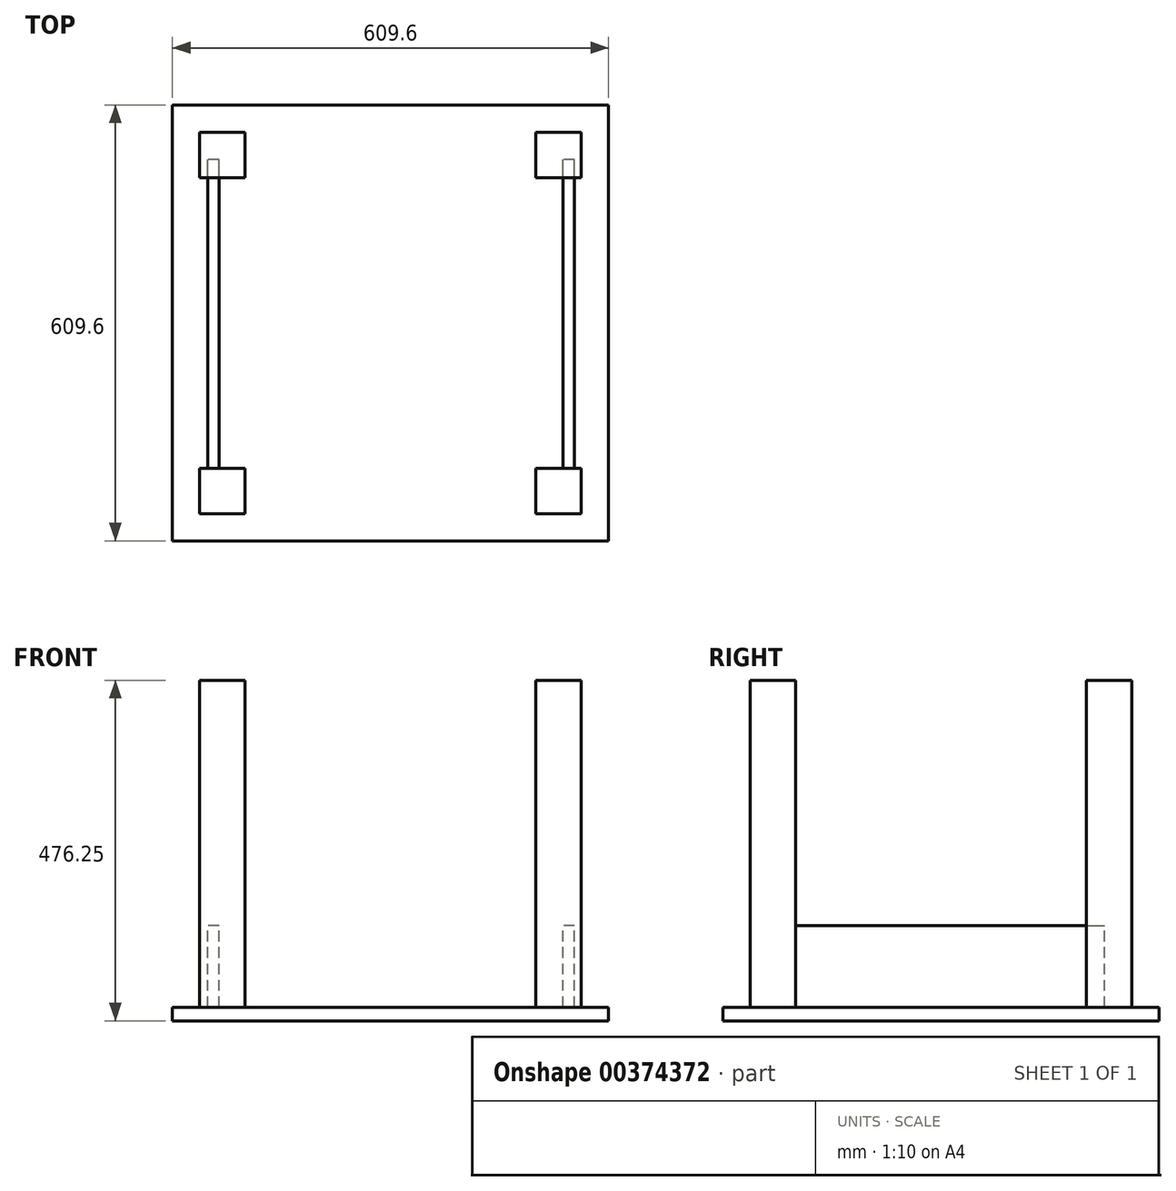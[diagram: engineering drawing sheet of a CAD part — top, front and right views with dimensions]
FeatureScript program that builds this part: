
annotation { "Feature Type Name" : "Feature", "Feature Type Description" : "" }
export const myFeature = defineFeature(function(context is Context, id is Id, definition is map)
    precondition{}
    {
        {
            var Q0;
            Q0=qCreatedBy(makeId("Front.planeOp"),FACE);
            var sketch = newSketch(context, id + "F0", { "sketchPlane" : qUnion([Q0])});
            skLineSegment(sketch, "E0.bottom", {"start": v(-303.33, -19.05) * mm, "end": v(306.27, -19.05) * mm});
            skLineSegment(sketch, "E0.top", {"start": v(-303.33, 0) * mm, "end": v(306.27, 0) * mm});
            skLineSegment(sketch, "E0.left", {"start": v(-303.33, -19.05) * mm, "end": v(-303.33, 0) * mm});
            skLineSegment(sketch, "E0.right", {"start": v(306.27, -19.05) * mm, "end": v(306.27, 0) * mm});
            skLineSegment(sketch, "E1.bottom", {"start": v(306.27, 0) * mm, "end": v(306.27, 0) * mm});
            skLineSegment(sketch, "E1.top", {"start": v(306.27, -19.05) * mm, "end": v(306.27, -19.05) * mm});
            skLineSegment(sketch, "E1.left", {"start": v(306.27, 0) * mm, "end": v(306.27, -19.05) * mm});
            skLineSegment(sketch, "E1.right", {"start": v(306.27, 0) * mm, "end": v(306.27, -19.05) * mm});
            skSolve(sketch);
        }
        {
            var Q0;
            Q0=makeQuery(id+"F0.imprint","IMPRINT",FACE,{"disambiguationData":[TD([[makeQuery(id+"F0.imprint","IMPRINT",EDGE,{"derivedFrom":sQuery(id+"F0.wireOp",EDGE,"E0.bottom")}),1.0]])]});
            extrude(context, id + "F1", {"entities" : qUnion([Q0]), "depth" : 609.6 * mm});
        }
        {
            var Q0;
            Q0=makeQuery(id+"F1.opExtrude","SWEPT_FACE",FACE,{"disambiguationData":[OSD([sQuery(id+"F0.wireOp",EDGE,"E0.top")])]});
            var sketch = newSketch(context, id + "F2", { "sketchPlane" : qUnion([Q0])});
            skLineSegment(sketch, "E2.bottom", {"start": v(-265.23, -571.5) * mm, "end": v(-201.73, -571.5) * mm});
            skLineSegment(sketch, "E2.top", {"start": v(-265.23, -508) * mm, "end": v(-201.73, -508) * mm});
            skLineSegment(sketch, "E2.left", {"start": v(-265.23, -571.5) * mm, "end": v(-265.23, -508) * mm});
            skLineSegment(sketch, "E2.right", {"start": v(-201.73, -571.5) * mm, "end": v(-201.73, -508) * mm});
            skLineSegment(sketch, "E3.bottom", {"start": v(-265.23, -38.1) * mm, "end": v(-201.73, -38.1) * mm});
            skLineSegment(sketch, "E3.top", {"start": v(-265.23, -101.6) * mm, "end": v(-201.73, -101.6) * mm});
            skLineSegment(sketch, "E3.left", {"start": v(-265.23, -38.1) * mm, "end": v(-265.23, -101.6) * mm});
            skLineSegment(sketch, "E3.right", {"start": v(-201.73, -38.1) * mm, "end": v(-201.73, -101.6) * mm});
            skLineSegment(sketch, "E4.bottom", {"start": v(268.17, -38.1) * mm, "end": v(204.67, -38.1) * mm});
            skLineSegment(sketch, "E4.top", {"start": v(268.17, -101.6) * mm, "end": v(204.67, -101.6) * mm});
            skLineSegment(sketch, "E4.left", {"start": v(268.17, -38.1) * mm, "end": v(268.17, -101.6) * mm});
            skLineSegment(sketch, "E4.right", {"start": v(204.67, -38.1) * mm, "end": v(204.67, -101.6) * mm});
            skLineSegment(sketch, "E5.bottom", {"start": v(268.17, -571.5) * mm, "end": v(204.67, -571.5) * mm});
            skLineSegment(sketch, "E5.top", {"start": v(268.17, -508) * mm, "end": v(204.67, -508) * mm});
            skLineSegment(sketch, "E5.left", {"start": v(268.17, -571.5) * mm, "end": v(268.17, -508) * mm});
            skLineSegment(sketch, "E5.right", {"start": v(204.67, -571.5) * mm, "end": v(204.67, -508) * mm});
            skSolve(sketch);
        }
        {
            var Q0;
            Q0=makeQuery(id+"F2.imprint","IMPRINT",FACE,{"disambiguationData":[TD([[makeQuery(id+"F2.imprint","IMPRINT",EDGE,{"derivedFrom":sQuery(id+"F2.wireOp",EDGE,"E2.bottom")}),1.0]])]});
            var Q1;
            Q1=makeQuery(id+"F2.imprint","IMPRINT",FACE,{"disambiguationData":[TD([[makeQuery(id+"F2.imprint","IMPRINT",EDGE,{"derivedFrom":sQuery(id+"F2.wireOp",EDGE,"E3.bottom")}),-1.0]])]});
            var Q2;
            Q2=makeQuery(id+"F2.imprint","IMPRINT",FACE,{"disambiguationData":[TD([[makeQuery(id+"F2.imprint","IMPRINT",EDGE,{"derivedFrom":sQuery(id+"F2.wireOp",EDGE,"E4.bottom")}),1.0]])]});
            var Q3;
            Q3=makeQuery(id+"F2.imprint","IMPRINT",FACE,{"disambiguationData":[TD([[makeQuery(id+"F2.imprint","IMPRINT",EDGE,{"derivedFrom":sQuery(id+"F2.wireOp",EDGE,"E5.bottom")}),-1.0]])]});
            extrude(context, id + "F3", {"entities" : qUnion([Q0, Q1, Q2, Q3]), "depth" : 457.2 * mm});
        }
        {
            var Q0;
            Q0=makeQuery(id+"F3.opExtrude","SWEPT_FACE",FACE,{"disambiguationData":[OSD([sQuery(id+"F2.wireOp",EDGE,"E4.top")])]});
            var sketch = newSketch(context, id + "F4", { "sketchPlane" : qUnion([Q0])});
            skLineSegment(sketch, "E6.bottom", {"start": v(258.64, 0) * mm, "end": v(242.77, 0) * mm});
            skLineSegment(sketch, "E6.top", {"start": v(258.64, 114.3) * mm, "end": v(242.77, 114.3) * mm});
            skLineSegment(sketch, "E6.left", {"start": v(258.64, 0) * mm, "end": v(258.64, 114.3) * mm});
            skLineSegment(sketch, "E6.right", {"start": v(242.77, 0) * mm, "end": v(242.77, 114.3) * mm});
            skSolve(sketch);
        }
        {
            var Q0;
            Q0=makeQuery(id+"F4.imprint","IMPRINT",FACE,{"disambiguationData":[TD([[makeQuery(id+"F4.imprint","IMPRINT",EDGE,{"derivedFrom":sQuery(id+"F4.wireOp",EDGE,"E6.bottom")}),-1.0]])]});
            extrude(context, id + "F5", {"entities" : qUnion([Q0]), "endBound" : BoundingType.UP_TO_NEXT, "depth" : 326.18 * mm, "hasSecondDirection" : true, "secondDirectionOppositeDirection" : true, "secondDirectionDepth" : 25.4 * mm});
        }
        {
            var Q0;
            Q0=makeQuery(id+"F5.opExtrude","SWEPT_BODY",BODY,{"disambiguationData":[OSD([sQuery(id+"F4.wireOp",EDGE,"E6.bottom"),sQuery(id+"F4.wireOp",EDGE,"E6.top"),sQuery(id+"F4.wireOp",EDGE,"E6.left"),sQuery(id+"F4.wireOp",EDGE,"E6.right")])]});
            transform(context, id + "F6", {"entities" : qUnion([Q0]), "transformType" : TransformType.TRANSLATION_3D, "dx" : -496.92 * mm, "dy" : 0 * mm, "dz" : 0 * mm, "makeCopy" : true});
        }
    });
